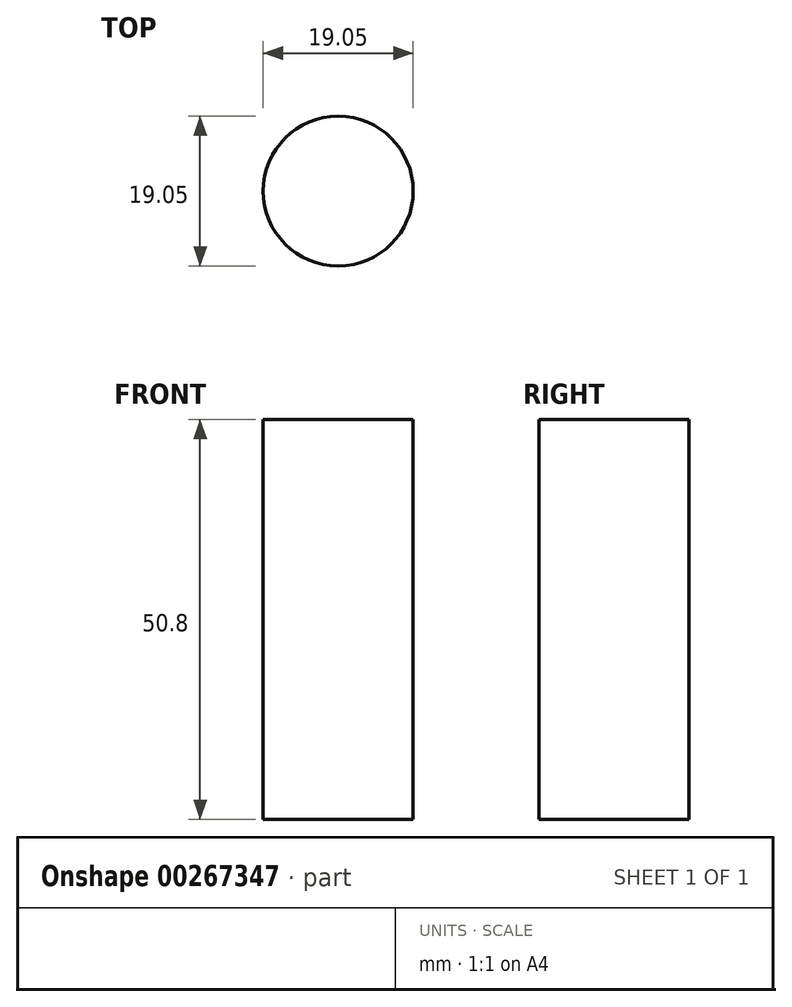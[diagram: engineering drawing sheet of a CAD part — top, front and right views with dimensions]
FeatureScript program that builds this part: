
annotation { "Feature Type Name" : "Feature", "Feature Type Description" : "" }
export const myFeature = defineFeature(function(context is Context, id is Id, definition is map)
    precondition{}
    {
        {
            var Q0;
            Q0=qCreatedBy(makeId("Top.planeOp"),FACE);
            var sketch = newSketch(context, id + "F0", { "sketchPlane" : qUnion([Q0])});
            skCircle(sketch, "E0", {"center": v(-65.12, -42.68) * mm, "radius": 9.53 * mm});
            skSolve(sketch);
        }
        {
            var Q0;
            Q0=makeQuery(id+"F0.imprint","IMPRINT",FACE,{"disambiguationData":[TD([[makeQuery(id+"F0.imprint","IMPRINT",EDGE,{"derivedFrom":sQuery(id+"F0.wireOp",EDGE,"E0")}),1.0]])]});
            extrude(context, id + "F1", {"entities" : qUnion([Q0]), "depth" : 50.8 * mm});
        }
    });
